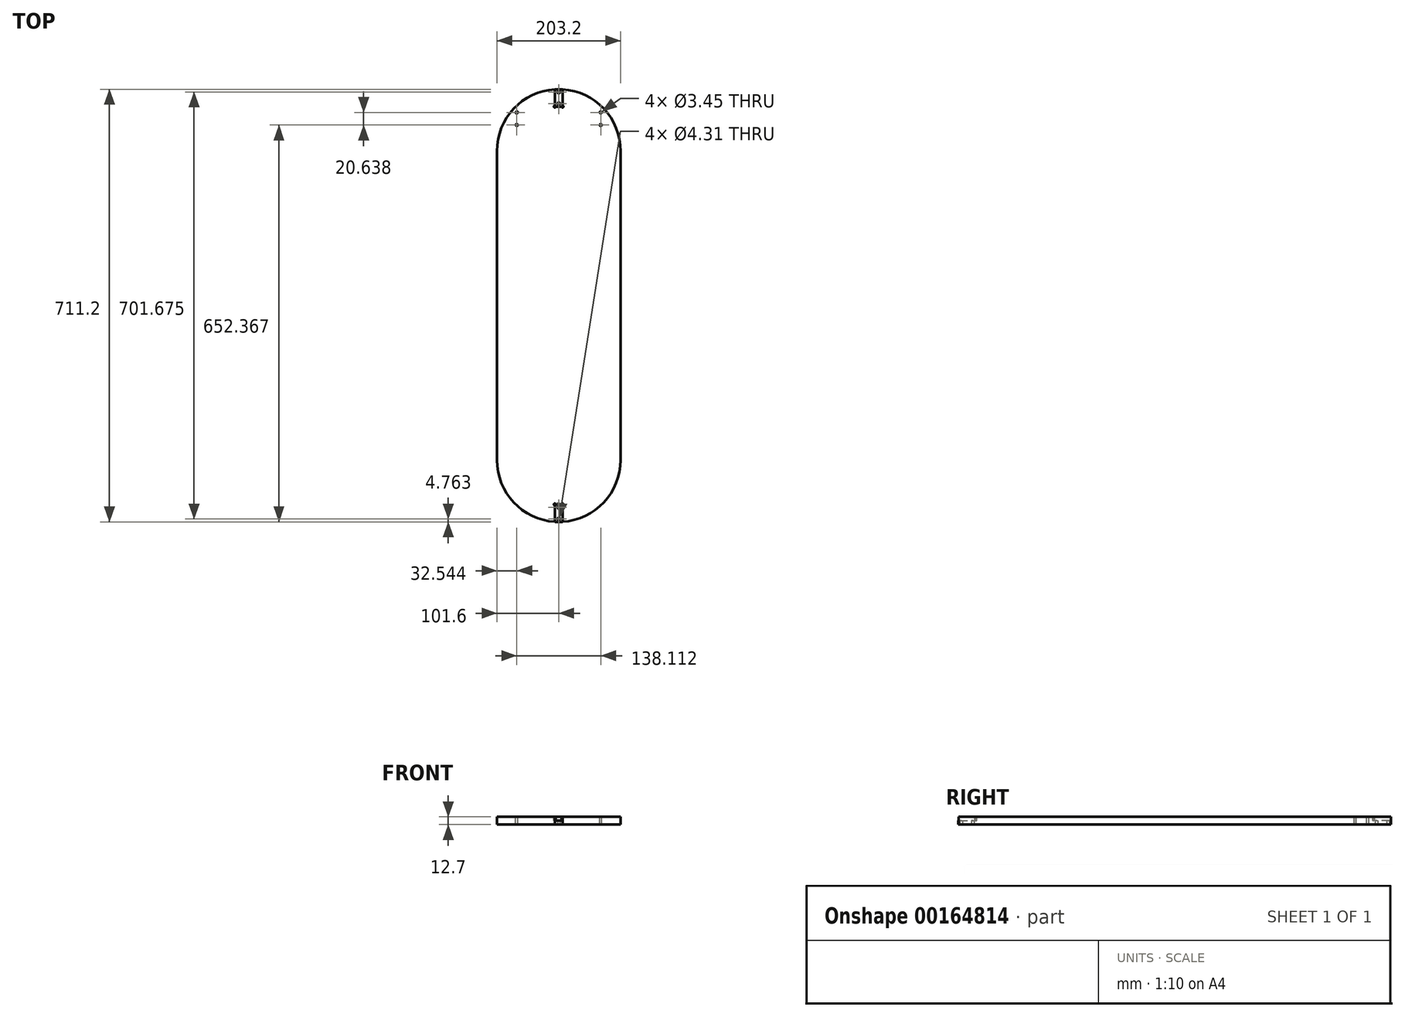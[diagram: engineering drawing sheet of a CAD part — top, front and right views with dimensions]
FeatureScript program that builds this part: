
annotation { "Feature Type Name" : "Feature", "Feature Type Description" : "" }
export const myFeature = defineFeature(function(context is Context, id is Id, definition is map)
    precondition{}
    {
        {
            var Q0;
            Q0=qCreatedBy(makeId("Top.planeOp"),FACE);
            var sketch = newSketch(context, id + "F0", { "sketchPlane" : qUnion([Q0])});
            skLineSegment(sketch, "E0.bottom", {"start": v(0, 0) * mm, "end": v(-203.2, 0) * mm, "construction": true});
            skLineSegment(sketch, "E0.top", {"start": v(0, -508) * mm, "end": v(-203.2, -508) * mm, "construction": true});
            skLineSegment(sketch, "E0.left", {"start": v(0, 0) * mm, "end": v(0, -508) * mm});
            skLineSegment(sketch, "E0.right", {"start": v(-203.2, 0) * mm, "end": v(-203.2, -508) * mm});
            skArc(sketch, "E1", {"start": v(-107.95, 101.4) * mm, "mid": v(-175.65, 69.56) * mm, "end": v(-203.2, 0) * mm});
            skArc(sketch, "E2", {"start": v(0, 0) * mm, "mid": v(-27.55, 69.56) * mm, "end": v(-95.25, 101.4) * mm});
            skLineSegment(sketch, "E3.bottom", {"start": v(-107.95, 101.4) * mm, "end": v(-95.25, 101.4) * mm, "construction": true});
            skLineSegment(sketch, "E3.top", {"start": v(-107.95, 101.6) * mm, "end": v(-95.25, 101.6) * mm});
            skLineSegment(sketch, "E3.left", {"start": v(-107.95, 101.4) * mm, "end": v(-107.95, 101.6) * mm});
            skLineSegment(sketch, "E3.right", {"start": v(-95.25, 101.4) * mm, "end": v(-95.25, 101.6) * mm});
            skLineSegment(sketch, "E4", {"start": v(-101.6, 101.4) * mm, "end": v(-101.6, 0) * mm, "construction": true});
            skArc(sketch, "E5", {"start": v(-95.25, 101.4) * mm, "mid": v(-101.6, 101.6) * mm, "end": v(-107.95, 101.4) * mm, "construction": true});
            skArc(sketch, "E6", {"start": v(-203.2, -508) * mm, "mid": v(-175.65, -577.56) * mm, "end": v(-107.95, -609.4) * mm});
            skArc(sketch, "E7", {"start": v(-95.25, -609.4) * mm, "mid": v(-27.55, -577.56) * mm, "end": v(0, -508) * mm});
            skLineSegment(sketch, "E8.bottom", {"start": v(-107.95, -609.4) * mm, "end": v(-95.25, -609.4) * mm, "construction": true});
            skLineSegment(sketch, "E8.top", {"start": v(-107.95, -609.6) * mm, "end": v(-95.25, -609.6) * mm});
            skLineSegment(sketch, "E8.left", {"start": v(-107.95, -609.4) * mm, "end": v(-107.95, -609.6) * mm});
            skLineSegment(sketch, "E8.right", {"start": v(-95.25, -609.4) * mm, "end": v(-95.25, -609.6) * mm});
            skLineSegment(sketch, "E9", {"start": v(-101.6, -508) * mm, "end": v(-101.6, -609.4) * mm, "construction": true});
            skSolve(sketch);
        }
        {
            var Q0;
            Q0=qSketchRegion(id+"F0",true);
            extrude(context, id + "F1", {"entities" : qUnion([Q0]), "depth" : 12.7 * mm});
        }
        {
            var Q0;
            Q0=makeQuery(id+"F1.opExtrude","CAP_FACE",FACE,{"disambiguationData":[OSD([sQuery(id+"F0.wireOp",EDGE,"E0.top"),sQuery(id+"F0.wireOp",EDGE,"E0.left"),sQuery(id+"F0.wireOp",EDGE,"E0.right"),sQuery(id+"F0.wireOp",EDGE,"SqmiRByB-BWnK-mEMi-qFd4-4WnWEakNxxXd"),sQuery(id+"F0.wireOp",EDGE,"jWmXs5kq-5ELT-ZpDA-D124-8Izf0WwcNPap")])],"isStart":false});
            var sketch = newSketch(context, id + "F2", { "sketchPlane" : qUnion([Q0])});
            skLineSegment(sketch, "E10.bottom", {"start": v(-170.66, 63.4) * mm, "end": v(-32.54, 63.4) * mm, "construction": true});
            skLineSegment(sketch, "E10.top", {"start": v(-170.66, 42.77) * mm, "end": v(-32.54, 42.77) * mm, "construction": true});
            skLineSegment(sketch, "E10.left", {"start": v(-170.66, 63.4) * mm, "end": v(-170.66, 42.77) * mm, "construction": true});
            skLineSegment(sketch, "E10.right", {"start": v(-32.54, 63.4) * mm, "end": v(-32.54, 42.77) * mm, "construction": true});
            skLineSegment(sketch, "E11", {"start": v(-32.54, 63.4) * mm, "end": v(-26.99, 63.4) * mm, "construction": true});
            skLineSegment(sketch, "E12", {"start": v(-26.99, 63.4) * mm, "end": v(-26.99, 68.96) * mm, "construction": true});
            skCircle(sketch, "E13", {"center": v(-32.54, 63.4) * mm, "radius": 1.73 * mm});
            skCircle(sketch, "E14", {"center": v(-32.54, 42.77) * mm, "radius": 1.73 * mm});
            skCircle(sketch, "E15", {"center": v(-170.66, 42.77) * mm, "radius": 1.73 * mm});
            skCircle(sketch, "E16", {"center": v(-170.66, 63.4) * mm, "radius": 1.73 * mm});
            skLineSegment(sketch, "E17", {"start": v(-101.6, 63.4) * mm, "end": v(-101.6, 101.6) * mm, "construction": true});
            skSolve(sketch);
        }
        {
            var Q0;
            Q0=qSketchRegion(id+"F2",true);
            var Q1;
            Q1=makeQuery(id+"F1.opExtrude","CAP_FACE",FACE,{"disambiguationData":[OSD([sQuery(id+"F0.wireOp",EDGE,"E0.top"),sQuery(id+"F0.wireOp",EDGE,"E0.left"),sQuery(id+"F0.wireOp",EDGE,"E0.right"),sQuery(id+"F0.wireOp",EDGE,"SqmiRByB-BWnK-mEMi-qFd4-4WnWEakNxxXd"),sQuery(id+"F0.wireOp",EDGE,"jWmXs5kq-5ELT-ZpDA-D124-8Izf0WwcNPap")])],"isStart":true});
            extrude(context, id + "F3", {"entities" : qUnion([Q0]), "operationType" : NewBodyOperationType.REMOVE, "endBound" : BoundingType.UP_TO_SURFACE, "oppositeDirection" : true, "endBoundEntityFace" : qUnion([Q1]), "depth" : 25.4 * mm});
        }
        {
            var Q0;
            Q0=makeQuery(id+"F1.opExtrude","CAP_FACE",FACE,{"disambiguationData":[OSD([sQuery(id+"F0.wireOp",EDGE,"E0.left"),sQuery(id+"F0.wireOp",EDGE,"E0.right"),sQuery(id+"F0.wireOp",EDGE,"NMU7Lit5-TsXM-QWri-J5EO-5gcQdLAaxlBr"),sQuery(id+"F0.wireOp",EDGE,"TDmExl8J-DLyR-47wp-Aw38-0aHgPelyYVzx")])],"isStart":false});
            var sketch = newSketch(context, id + "F4", { "sketchPlane" : qUnion([Q0])});
            skLineSegment(sketch, "E18.bottom", {"start": v(-107.95, 101.6) * mm, "end": v(-95.25, 101.6) * mm});
            skLineSegment(sketch, "E18.top", {"start": v(-107.95, 73.02) * mm, "end": v(-95.25, 73.02) * mm});
            skLineSegment(sketch, "E18.left", {"start": v(-107.95, 101.6) * mm, "end": v(-107.95, 73.02) * mm});
            skLineSegment(sketch, "E18.right", {"start": v(-95.25, 101.6) * mm, "end": v(-95.25, 73.02) * mm});
            skLineSegment(sketch, "E19.bottom", {"start": v(-107.95, -609.6) * mm, "end": v(-95.25, -609.6) * mm});
            skLineSegment(sketch, "E19.top", {"start": v(-107.95, -581.02) * mm, "end": v(-95.25, -581.02) * mm});
            skLineSegment(sketch, "E19.left", {"start": v(-107.95, -609.6) * mm, "end": v(-107.95, -581.02) * mm});
            skLineSegment(sketch, "E19.right", {"start": v(-95.25, -609.6) * mm, "end": v(-95.25, -581.02) * mm});
            skLineSegment(sketch, "E20", {"start": v(-101.6, 73.02) * mm, "end": v(-101.6, -581.02) * mm, "construction": true});
            skLineSegment(sketch, "E21", {"start": v(-203.2, -254) * mm, "end": v(-101.6, -254) * mm, "construction": true});
            skLineSegment(sketch, "E22", {"start": v(-101.6, -254) * mm, "end": v(0, -254) * mm, "construction": true});
            skSolve(sketch);
        }
        {
            var Q0;
            Q0 = qSketchRegion(id + "F4", true);
            extrude(context, id + "F5", {"entities" : qUnion([Q0]), "operationType" : NewBodyOperationType.REMOVE, "oppositeDirection" : true, "depth" : 6.35 * mm});
        }
        {
            var Q0;
            Q0=makeQuery(id+"F1.opExtrude","CAP_FACE",FACE,{"disambiguationData":[OSD([sQuery(id+"F0.wireOp",EDGE,"E0.left"),sQuery(id+"F0.wireOp",EDGE,"E0.right"),sQuery(id+"F0.wireOp",EDGE,"NMU7Lit5-TsXM-QWri-J5EO-5gcQdLAaxlBr"),sQuery(id+"F0.wireOp",EDGE,"TDmExl8J-DLyR-47wp-Aw38-0aHgPelyYVzx")])],"isStart":false});
            var sketch = newSketch(context, id + "F6", { "sketchPlane" : qUnion([Q0])});
            skCircle(sketch, "E23", {"center": v(-107.95, -581.02) * mm, "radius": 1.59 * mm});
            skCircle(sketch, "E24", {"center": v(-95.25, -581.02) * mm, "radius": 1.59 * mm});
            skCircle(sketch, "E25", {"center": v(-107.95, 73.02) * mm, "radius": 1.59 * mm});
            skCircle(sketch, "E26", {"center": v(-95.25, 73.02) * mm, "radius": 1.59 * mm});
            skSolve(sketch);
        }
        {
            var Q0;
            Q0 = qSketchRegion(id + "F6", true);
            var Q1;
            Q1=makeQuery(id+"F5.boolean.opBoolean","COPY",FACE,{"derivedFrom":makeQuery(id+"F5.opExtrude","CAP_FACE",FACE,{"disambiguationData":[OSD([sQuery(id+"F4.wireOp",EDGE,"E18.bottom"),sQuery(id+"F4.wireOp",EDGE,"E18.top"),sQuery(id+"F4.wireOp",EDGE,"E18.left"),sQuery(id+"F4.wireOp",EDGE,"E18.right")])],"isStart":false})});
            extrude(context, id + "F7", {"entities" : qUnion([Q0]), "operationType" : NewBodyOperationType.REMOVE, "endBound" : BoundingType.UP_TO_SURFACE, "oppositeDirection" : true, "endBoundEntityFace" : qUnion([Q1]), "depth" : 25.4 * mm});
        }
        {
            var Q0;
            Q0=makeQuery(id+"F1.opExtrude","CAP_FACE",FACE,{"disambiguationData":[OSD([sQuery(id+"F0.wireOp",EDGE,"E0.left"),sQuery(id+"F0.wireOp",EDGE,"E0.right"),sQuery(id+"F0.wireOp",EDGE,"NMU7Lit5-TsXM-QWri-J5EO-5gcQdLAaxlBr"),sQuery(id+"F0.wireOp",EDGE,"TDmExl8J-DLyR-47wp-Aw38-0aHgPelyYVzx")])],"isStart":true});
            var sketch = newSketch(context, id + "F8", { "sketchPlane" : qUnion([Q0])});
            skLineSegment(sketch, "E27", {"start": v(-101.6, -101.6) * mm, "end": v(-101.6, -96.84) * mm, "construction": true});
            skLineSegment(sketch, "E28", {"start": v(-101.6, -96.84) * mm, "end": v(-101.6, -77.79) * mm, "construction": true});
            skLineSegment(sketch, "E29", {"start": v(-101.6, -77.79) * mm, "end": v(-101.6, 585.79) * mm, "construction": true});
            skLineSegment(sketch, "E30", {"start": v(-101.6, 585.79) * mm, "end": v(-101.6, 604.84) * mm, "construction": true});
            skLineSegment(sketch, "E31", {"start": v(-101.6, 604.84) * mm, "end": v(-101.6, 609.6) * mm, "construction": true});
            skCircle(sketch, "E32", {"center": v(-101.6, -96.84) * mm, "radius": 2.15 * mm});
            skCircle(sketch, "E33", {"center": v(-101.6, -77.79) * mm, "radius": 2.15 * mm});
            skCircle(sketch, "E34", {"center": v(-101.6, 604.84) * mm, "radius": 2.15 * mm});
            skCircle(sketch, "E35", {"center": v(-101.6, 585.79) * mm, "radius": 2.15 * mm});
            skSolve(sketch);
        }
        {
            var Q0;
            Q0 = qSketchRegion(id + "F8", true);
            var Q1;
            Q1=makeQuery(id+"F1.opExtrude","CAP_FACE",FACE,{"disambiguationData":[OSD([sQuery(id+"F0.wireOp",EDGE,"E0.left"),sQuery(id+"F0.wireOp",EDGE,"E0.right"),sQuery(id+"F0.wireOp",EDGE,"NMU7Lit5-TsXM-QWri-J5EO-5gcQdLAaxlBr"),sQuery(id+"F0.wireOp",EDGE,"TDmExl8J-DLyR-47wp-Aw38-0aHgPelyYVzx")])],"isStart":false});
            extrude(context, id + "F9", {"entities" : qUnion([Q0]), "operationType" : NewBodyOperationType.REMOVE, "endBound" : BoundingType.UP_TO_SURFACE, "oppositeDirection" : true, "endBoundEntityFace" : qUnion([Q1]), "depth" : 25.4 * mm});
        }
    });
